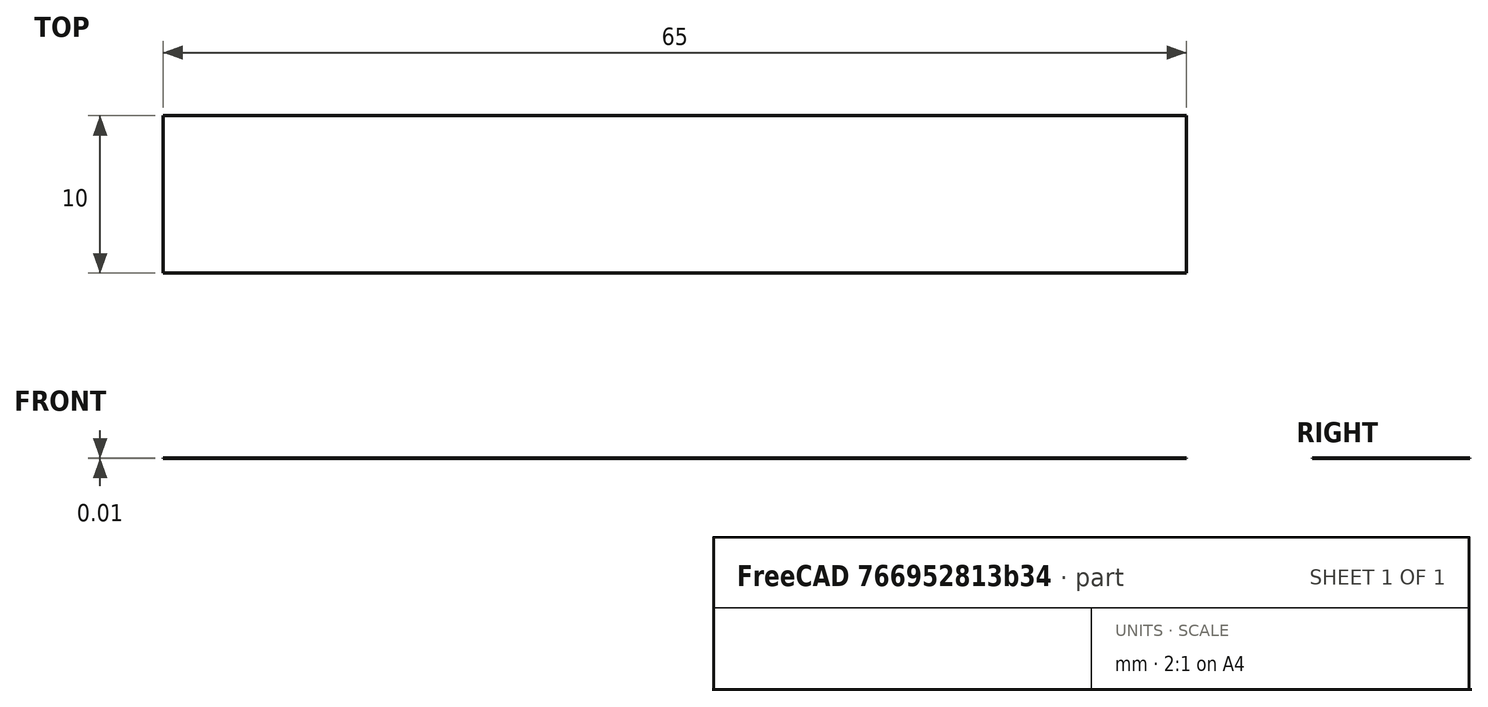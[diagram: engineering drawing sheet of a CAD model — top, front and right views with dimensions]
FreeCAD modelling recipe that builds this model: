
FCSTD DOCUMENT  (FreeCAD 0.19R23058 (Git))
Label: label_1
License: All rights reserved
LicenseURL: http://en.wikipedia.org/wiki/All_rights_reserved
objects: App::MaterialObjectPython×1, Part::Box×1, PartDesign::Point×1, App::DocumentObjectGroupPython×1, App::FeaturePython×1
note: 2 computed .brp shape members not serialized (recipe doc carries the construction recipe); baked Part::Feature solids carry a one-line shape summary decoded from their .brp

FEATURE [App::MaterialObjectPython] Material  label="Label"  # material (typed FeaturePython)
  Description = This is a blend AcrylnitrilButadienStyrol (ABS) material card. The values are at the low end of the spectrum. If you need a more precise material definition use the more specialised ABS-blend cards.
  Material = AuthorAndLicense=ABS-Generic,CardName=ABS-Generic,Color=(0.8, 0.8, 0.8, 1.0),Density=1060 kg/m^3,+16 more (map truncated)
  ProductURL = https://en.wikipedia.org/wiki/Acrylonitrile_butadiene_styrene
  Transparency = 0
FEATURE [Part::Box] Box  label="Куб"
  AttacherType = Attacher::AttachEngine3D
  Height = 0.01
  Length = 65
  Material = -> Material
  Width = 10
FEATURE [PartDesign::Point] Point_1
  AttacherType = Attacher::AttachEnginePoint
  MapMode = 39
  Placement = pos=(65,10,0) rot=(0,0,1;0rad)
  Support = -> [Box]
FEATURE [App::DocumentObjectGroupPython] MaterialContainer  label="Materials"  # scripted group (container) (typed FeaturePython)
  Group = -> [Material]
FEATURE [App::FeaturePython] TextureConfig  # WARN: FeaturePython — macro-defined, semantics opaque (R4)
